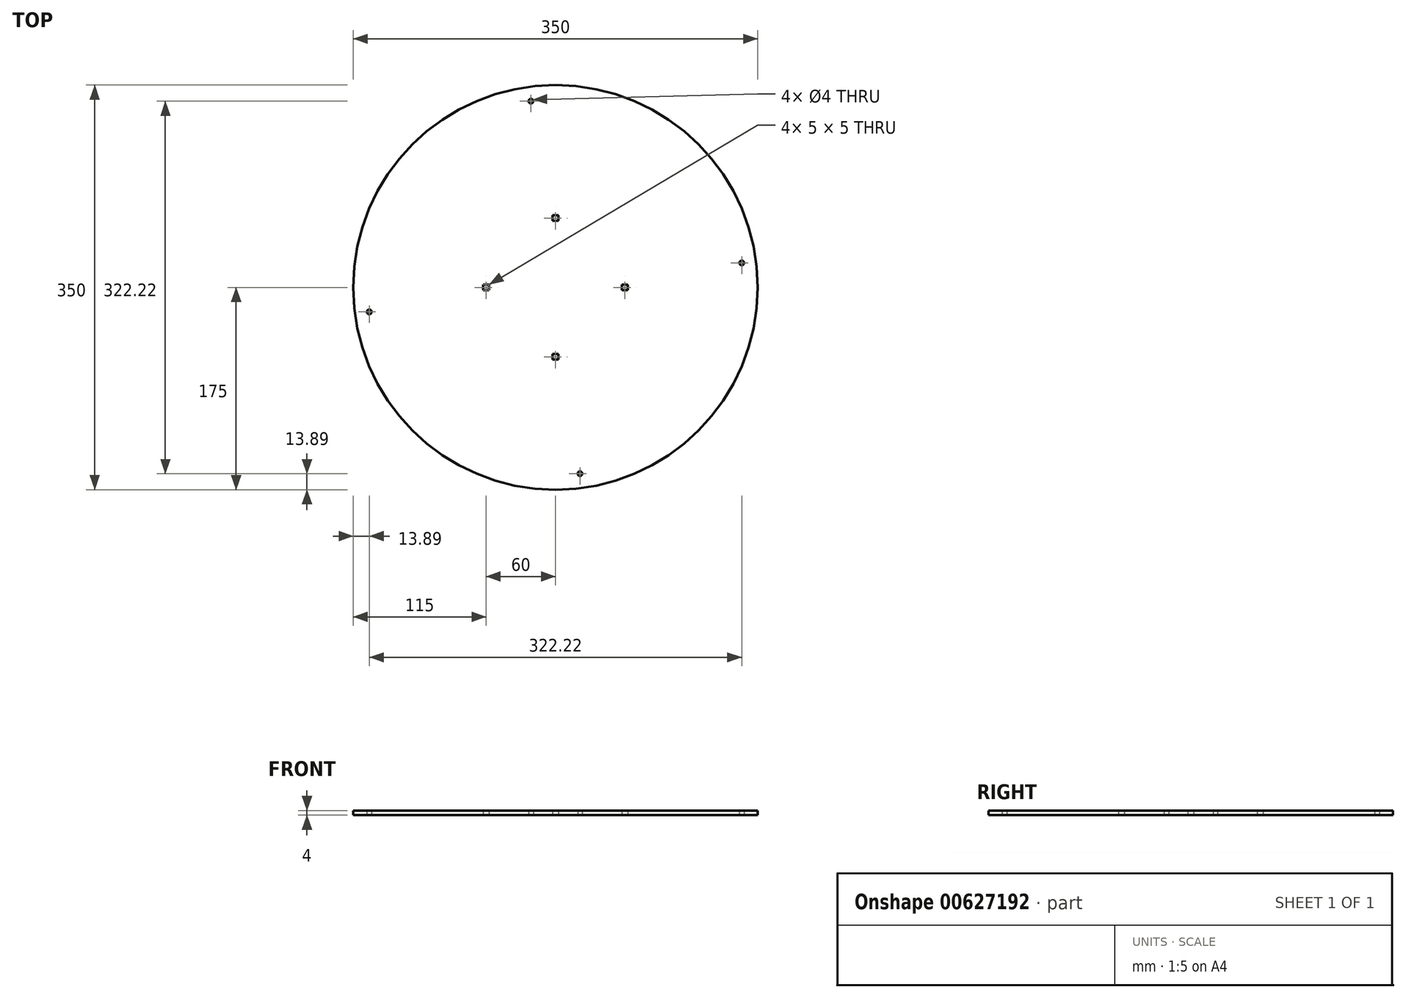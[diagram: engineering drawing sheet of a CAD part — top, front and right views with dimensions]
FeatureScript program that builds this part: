
annotation { "Feature Type Name" : "Feature", "Feature Type Description" : "" }
export const myFeature = defineFeature(function(context is Context, id is Id, definition is map)
    precondition{}
    {
        {
            var Q0;
            Q0=qCreatedBy(makeId("Top.planeOp"),FACE);
            var sketch = newSketch(context, id + "F0", { "sketchPlane" : qUnion([Q0])});
            skCircle(sketch, "E0", {"center": v(0, 0) * mm, "radius": 175 * mm});
            skLineSegment(sketch, "E1", {"start": v(0, 196.69) * mm, "end": v(0, -203.31) * mm, "construction": true});
            skLineSegment(sketch, "E2", {"start": v(-208.27, 0) * mm, "end": v(191.73, 0) * mm, "construction": true});
            skLineSegment(sketch, "E3.bottom", {"start": v(2.5, 57.5) * mm, "end": v(-2.5, 57.5) * mm});
            skLineSegment(sketch, "E3.top", {"start": v(2.5, 62.5) * mm, "end": v(-2.5, 62.5) * mm});
            skLineSegment(sketch, "E3.left", {"start": v(2.5, 57.5) * mm, "end": v(2.5, 62.5) * mm});
            skLineSegment(sketch, "E3.right", {"start": v(-2.5, 57.5) * mm, "end": v(-2.5, 62.5) * mm});
            skPoint(sketch, "E3.middle", {"position": v(0, 60) * mm});
            skLineSegment(sketch, "E4.bottom", {"start": v(62.5, -2.5) * mm, "end": v(57.5, -2.5) * mm});
            skLineSegment(sketch, "E4.top", {"start": v(62.5, 2.5) * mm, "end": v(57.5, 2.5) * mm});
            skLineSegment(sketch, "E4.left", {"start": v(62.5, -2.5) * mm, "end": v(62.5, 2.5) * mm});
            skLineSegment(sketch, "E4.right", {"start": v(57.5, -2.5) * mm, "end": v(57.5, 2.5) * mm});
            skPoint(sketch, "E4.middle", {"position": v(60, 0) * mm});
            skLineSegment(sketch, "E5.MirrorCS", {"start": v(-62.5, -2.5) * mm, "end": v(-62.5, 2.5) * mm});
            skLineSegment(sketch, "E6.MirrorCS", {"start": v(-62.5, 2.5) * mm, "end": v(-57.5, 2.5) * mm});
            skLineSegment(sketch, "E7.MirrorCS", {"start": v(-57.5, -2.5) * mm, "end": v(-57.5, 2.5) * mm});
            skLineSegment(sketch, "E8.MirrorCS", {"start": v(-62.5, -2.5) * mm, "end": v(-57.5, -2.5) * mm});
            skLineSegment(sketch, "E9.MirrorCS", {"start": v(-2.5, -57.5) * mm, "end": v(-2.5, -62.5) * mm});
            skLineSegment(sketch, "E10.MirrorCS", {"start": v(2.5, -57.5) * mm, "end": v(-2.5, -57.5) * mm});
            skLineSegment(sketch, "E11.MirrorCS", {"start": v(2.5, -57.5) * mm, "end": v(2.5, -62.5) * mm});
            skLineSegment(sketch, "E12.MirrorCS", {"start": v(2.5, -62.5) * mm, "end": v(-2.5, -62.5) * mm});
            skLineSegment(sketch, "E13", {"start": v(0, 0) * mm, "end": v(-24.52, 186.27) * mm, "construction": true});
            skLineSegment(sketch, "E14", {"start": v(0, 0) * mm, "end": v(23.5, -178.46) * mm, "construction": true});
            skLineSegment(sketch, "E15", {"start": v(0, 0) * mm, "end": v(178.46, 23.5) * mm, "construction": true});
            skLineSegment(sketch, "E16", {"start": v(0, 0) * mm, "end": v(-178.46, -23.5) * mm, "construction": true});
            skCircle(sketch, "E17", {"center": v(-21.21, 161.1) * mm, "radius": 2 * mm});
            skCircle(sketch, "E18", {"center": v(161.1, 21.21) * mm, "radius": 2 * mm});
            skCircle(sketch, "E19", {"center": v(21.21, -161.1) * mm, "radius": 2 * mm});
            skCircle(sketch, "E20", {"center": v(-161.1, -21.21) * mm, "radius": 2 * mm});
            skSolve(sketch);
        }
        {
            var Q0;
            Q0=makeQuery(id+"F0.imprint","IMPRINT",FACE,{"disambiguationData":[TD([[makeQuery(id+"F0.imprint","IMPRINT",EDGE,{"derivedFrom":sQuery(id+"F0.wireOp",EDGE,"E0")}),1.0]])]});
            extrude(context, id + "F1", {"entities" : qUnion([Q0]), "depth" : 4 * mm, "offsetDistance" : 25 * mm});
        }
    });
